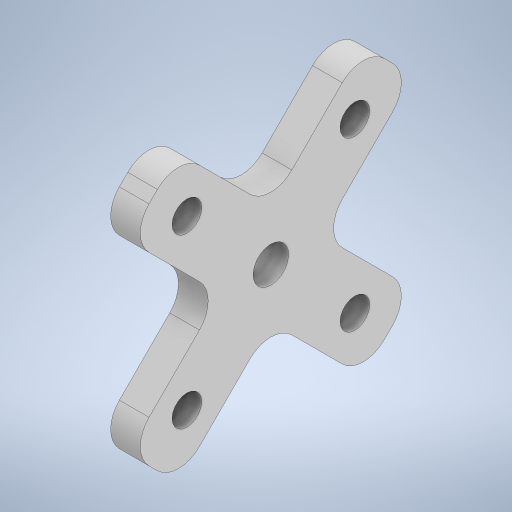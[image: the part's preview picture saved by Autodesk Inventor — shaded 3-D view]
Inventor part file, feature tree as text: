
AUTODESK INVENTOR PART (.ipt)
format: ipt  version: 2023 (Build 270158000, 158)  size: 296,960 bytes
history: native  units: in
note: dims shown in document units (in); Inventor stores cm internally (conversion verified against a paired STEP export)
features: extrude x1, fillet x1, sketch x1
ambient origin geometry x8: Origin, YZ Plane, XZ Plane, XY Plane, X Axis, Y Axis, Z Axis, Center Point
bodies: Solid1 (feature_tree)
feature tree (3):
  extrude  "Extrusion1"  Depth=1.414in
  fillet  "Fillet1"  Radius=0.3in
  sketch  "Sketch1"  dims[d0=1.414in d1=1.414in d2=0.3in d3=0.25in d4=0.25in d5=0.25in d6=0.25in d7=0.3in d8=1.4in d9=0.6in d10=1.4in d11=0.6in d12=1.4in d13=0.25in d14=0.0in d15=0.25in]
